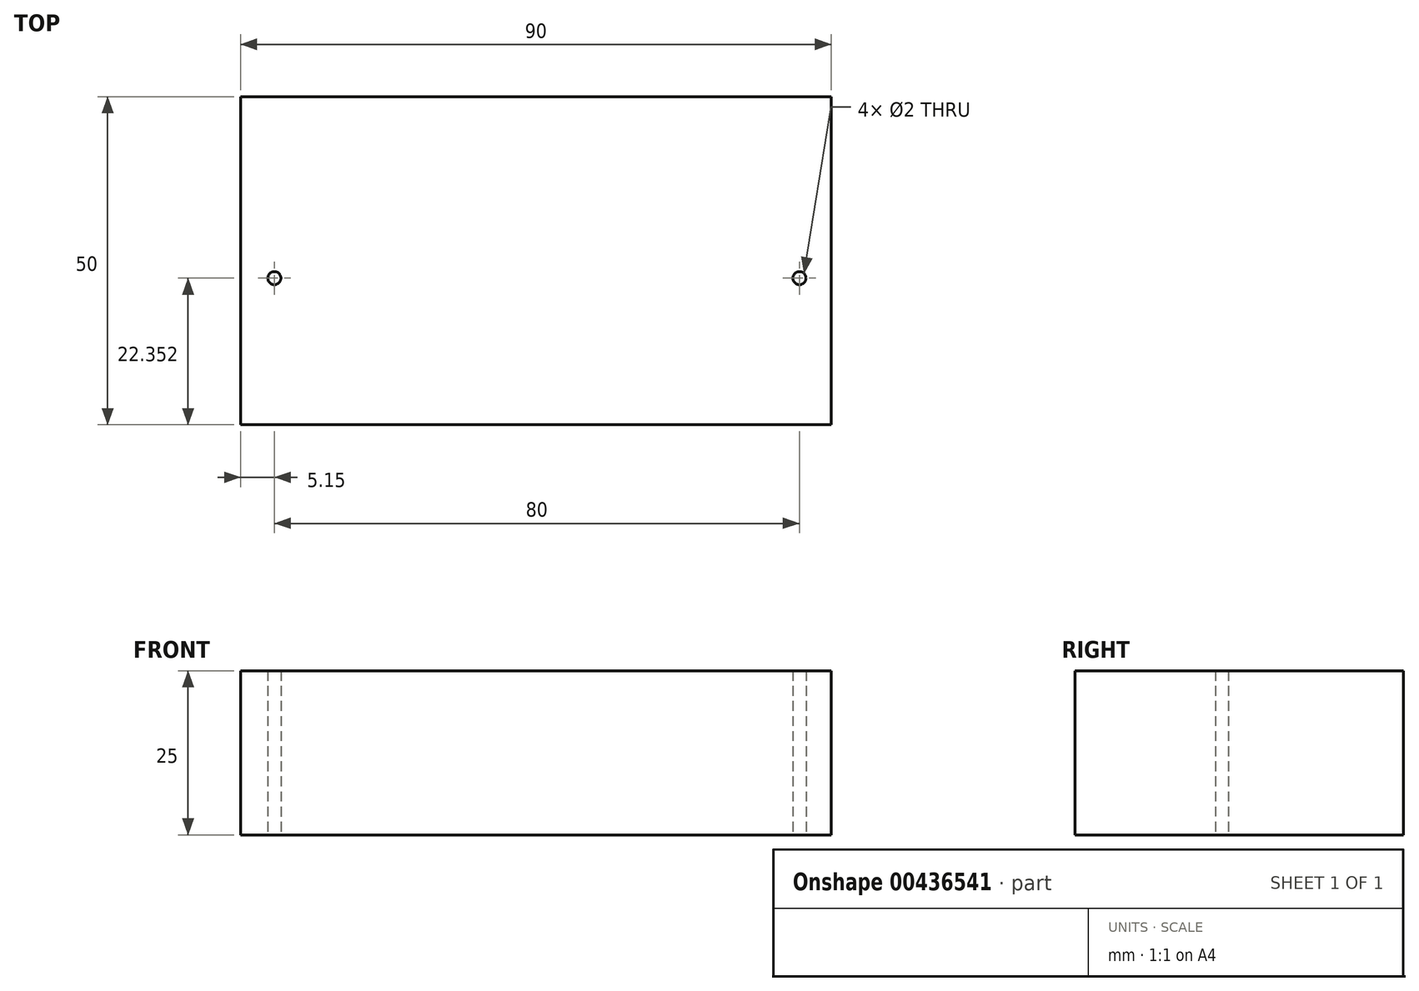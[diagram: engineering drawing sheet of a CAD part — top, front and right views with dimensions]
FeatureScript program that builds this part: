
annotation { "Feature Type Name" : "Feature", "Feature Type Description" : "" }
export const myFeature = defineFeature(function(context is Context, id is Id, definition is map)
    precondition{}
    {
        {
            var Q0;
            Q0=qCreatedBy(makeId("Top.planeOp"),FACE);
            var sketch = newSketch(context, id + "F0", { "sketchPlane" : qUnion([Q0])});
            skLineSegment(sketch, "E0.bottom", {"start": v(-32.02, 19.45) * mm, "end": v(57.98, 19.45) * mm});
            skLineSegment(sketch, "E0.top", {"start": v(-32.02, -30.55) * mm, "end": v(57.98, -30.55) * mm});
            skLineSegment(sketch, "E0.left", {"start": v(-32.02, 19.45) * mm, "end": v(-32.02, -30.55) * mm});
            skLineSegment(sketch, "E0.right", {"start": v(57.98, 19.45) * mm, "end": v(57.98, -30.55) * mm});
            skCircle(sketch, "E1", {"center": v(-26.87, -8.2) * mm, "radius": 1 * mm});
            skCircle(sketch, "E2", {"center": v(53.13, -8.2) * mm, "radius": 1 * mm});
            skSolve(sketch);
        }
        {
            var Q0;
            Q0=makeQuery(id+"F0.imprint","IMPRINT",FACE,{"disambiguationData":[TD([[makeQuery(id+"F0.imprint","IMPRINT",EDGE,{"derivedFrom":sQuery(id+"F0.wireOp",EDGE,"E0.bottom")}),-1.0]])]});
            extrude(context, id + "F1", {"entities" : qUnion([Q0]), "depth" : 25 * mm});
        }
    });
